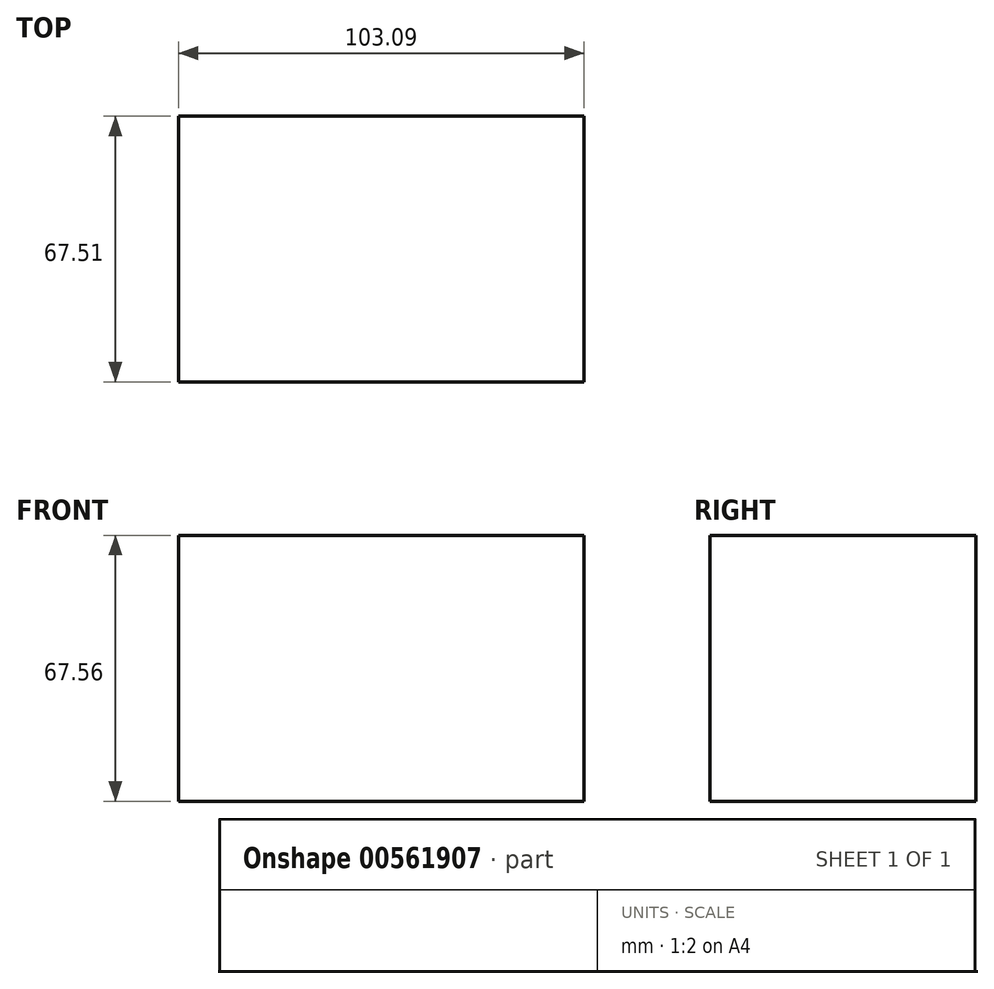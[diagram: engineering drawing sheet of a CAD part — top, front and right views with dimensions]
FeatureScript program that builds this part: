
annotation { "Feature Type Name" : "Feature", "Feature Type Description" : "" }
export const myFeature = defineFeature(function(context is Context, id is Id, definition is map)
    precondition{}
    {
        {
            var Q0;
            Q0=qCreatedBy(makeId("Top.planeOp"),FACE);
            var sketch = newSketch(context, id + "F0", { "sketchPlane" : qUnion([Q0])});
            skLineSegment(sketch, "E0.bottom", {"start": v(-46.16, 27.35) * mm, "end": v(56.93, 27.35) * mm});
            skLineSegment(sketch, "E0.top", {"start": v(-46.16, -40.16) * mm, "end": v(56.93, -40.16) * mm});
            skLineSegment(sketch, "E0.left", {"start": v(-46.16, 27.35) * mm, "end": v(-46.16, -40.16) * mm});
            skLineSegment(sketch, "E0.right", {"start": v(56.93, 27.35) * mm, "end": v(56.93, -40.16) * mm});
            skSolve(sketch);
        }
        {
            var Q0;
            Q0=makeQuery(id+"F0.imprint","IMPRINT",FACE,{"disambiguationData":[TD([[makeQuery(id+"F0.imprint","IMPRINT",EDGE,{"derivedFrom":sQuery(id+"F0.wireOp",EDGE,"E0.bottom")}),-1.0]])]});
            extrude(context, id + "F1", {"entities" : qUnion([Q0]), "depth" : 67.56 * mm, "offsetDistance" : 25.4 * mm});
        }
    });
